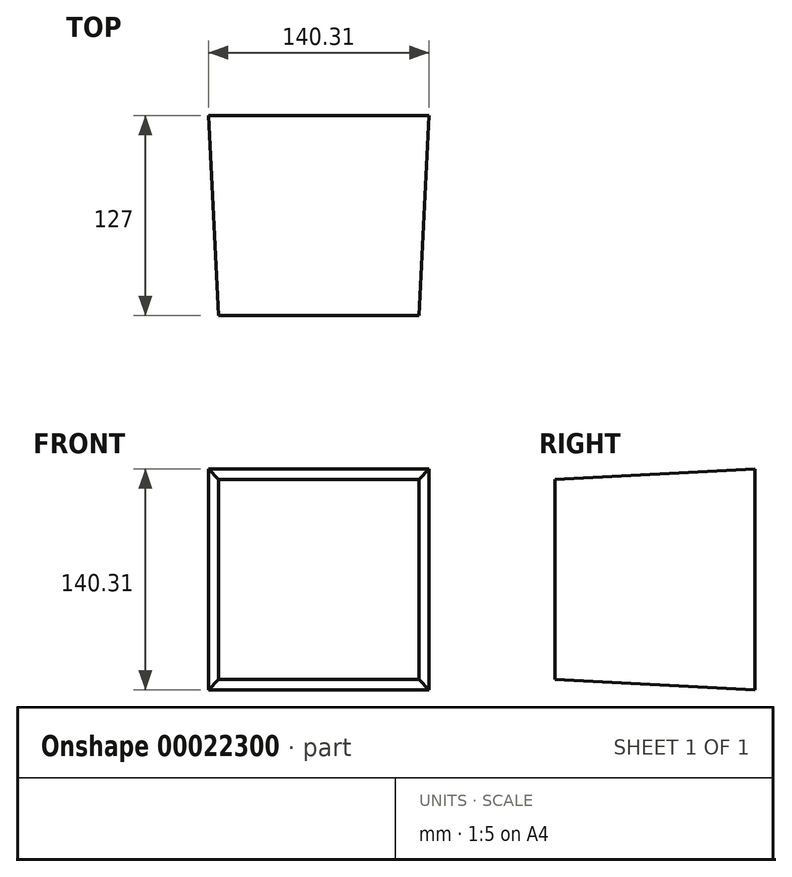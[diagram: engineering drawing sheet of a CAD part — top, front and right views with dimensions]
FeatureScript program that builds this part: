
annotation { "Feature Type Name" : "Feature", "Feature Type Description" : "" }
export const myFeature = defineFeature(function(context is Context, id is Id, definition is map)
    precondition{}
    {
        {
            var Q0;
            Q0=qCreatedBy(makeId("Front.planeOp"),FACE);
            var sketch = newSketch(context, id + "F0", { "sketchPlane" : qUnion([Q0])});
            skLineSegment(sketch, "E0", {"start": v(-80.13, 74.97) * mm, "end": v(46.87, 74.97) * mm});
            skLineSegment(sketch, "E1", {"start": v(46.87, 74.97) * mm, "end": v(46.87, -52.03) * mm});
            skLineSegment(sketch, "E2", {"start": v(46.87, -52.03) * mm, "end": v(-80.13, -52.03) * mm});
            skLineSegment(sketch, "E3", {"start": v(-80.13, -52.03) * mm, "end": v(-80.13, 74.97) * mm});
            skSolve(sketch);
        }
        {
            var Q0;
            Q0 = qSketchRegion(id + "F0", true);
            extrude(context, id + "F1", {"entities" : qUnion([Q0]), "oppositeDirection" : true, "depth" : 127 * mm, "hasDraft" : true, "draftAngle" : 3 * degree});
        }
    });
